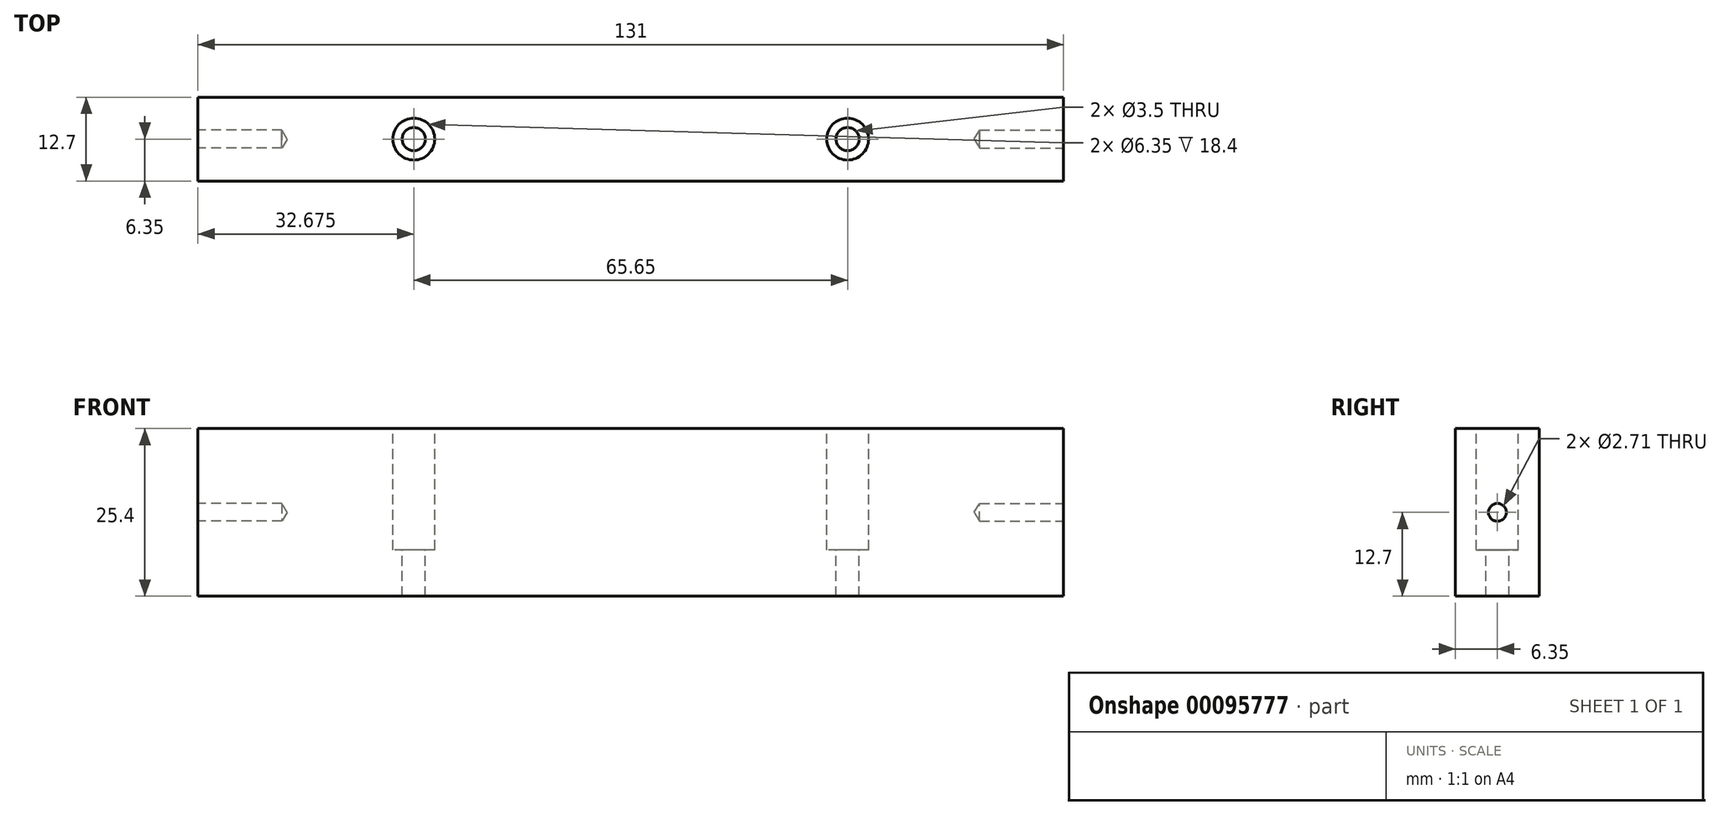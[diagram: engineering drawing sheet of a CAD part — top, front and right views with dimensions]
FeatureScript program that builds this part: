
annotation { "Feature Type Name" : "Feature", "Feature Type Description" : "" }
export const myFeature = defineFeature(function(context is Context, id is Id, definition is map)
    precondition{}
    {
        {
            var Q0;
            Q0=qCreatedBy(makeId("Right.planeOp"),FACE);
            var sketch = newSketch(context, id + "F0", { "sketchPlane" : qUnion([Q0])});
            skLineSegment(sketch, "E0.bottom", {"start": v(-6.35, -12.7) * mm, "end": v(6.35, -12.7) * mm});
            skLineSegment(sketch, "E0.top", {"start": v(-6.35, 12.7) * mm, "end": v(6.35, 12.7) * mm});
            skLineSegment(sketch, "E0.left", {"start": v(-6.35, -12.7) * mm, "end": v(-6.35, 12.7) * mm});
            skLineSegment(sketch, "E0.right", {"start": v(6.35, -12.7) * mm, "end": v(6.35, 12.7) * mm});
            skPoint(sketch, "E0.middle", {"position": v(0, 0) * mm});
            skSolve(sketch);
        }
        {
            var Q0;
            Q0 = qSketchRegion(id + "F0", true);
            extrude(context, id + "F1", {"entities" : qUnion([Q0]), "depth" : 131 * mm});
        }
        {
            var Q0;
            Q0=makeQuery(id+"F1.opExtrude","SWEPT_FACE",FACE,{"disambiguationData":[OSD([sQuery(id+"F0.wireOp",EDGE,"E0.top")])]});
            var sketch = newSketch(context, id + "F2", { "sketchPlane" : qUnion([Q0])});
            skPoint(sketch, "E1", {"position": v(32.67, 0) * mm});
            skPoint(sketch, "E2", {"position": v(98.33, 0) * mm});
            skLineSegment(sketch, "E3", {"start": v(65.5, -6.35) * mm, "end": v(65.5, 6.35) * mm, "construction": true});
            skSolve(sketch);
        }
        {
            var Q0;
            Q0=sQuery(id+"F2.wireOp",VERTEX,"E1");
            var Q1;
            Q1=sQuery(id+"F2.wireOp",VERTEX,"E2");
            var Q2;
            Q2=makeQuery(id+"F1.opExtrude","SWEPT_BODY",BODY,{"disambiguationData":[OSD([sQuery(id+"F0.wireOp",EDGE,"E0.bottom"),sQuery(id+"F0.wireOp",EDGE,"E0.top"),sQuery(id+"F0.wireOp",EDGE,"E0.left"),sQuery(id+"F0.wireOp",EDGE,"E0.right")])]});
            hole(context, id + "F3", {"style" : HoleStyle.C_BORE, "endStyle" : HoleEndStyle.THROUGH, "holeDiameter" : 3.5 * mm, "cBoreDiameter" : 6.35 * mm, "cBoreDepth" : 18.4 * mm, "startFromSketch" : true, "locations" : qUnion([Q0, Q1]), "scope" : qUnion([Q2]), "isTappedThrough" : true});
        }
        {
            var Q0;
            Q0=makeQuery(id+"F1.opExtrude","CAP_FACE",FACE,{"disambiguationData":[OSD([sQuery(id+"F0.wireOp",EDGE,"E0.bottom"),sQuery(id+"F0.wireOp",EDGE,"E0.top"),sQuery(id+"F0.wireOp",EDGE,"E0.left"),sQuery(id+"F0.wireOp",EDGE,"E0.right")])],"isStart":false});
            var sketch = newSketch(context, id + "F4", { "sketchPlane" : qUnion([Q0])});
            skLineSegment(sketch, "E4", {"start": v(-6.35, 0) * mm, "end": v(6.35, 0) * mm, "construction": true});
            skPoint(sketch, "E5", {"position": v(0, 0) * mm});
            skSolve(sketch);
        }
        {
            var Q0;
            Q0=sQuery(id+"F4.wireOp",VERTEX,"E5");
            var Q1;
            Q1=makeQuery(id+"F1.opExtrude","SWEPT_BODY",BODY,{"disambiguationData":[OSD([sQuery(id+"F0.wireOp",EDGE,"E0.bottom"),sQuery(id+"F0.wireOp",EDGE,"E0.top"),sQuery(id+"F0.wireOp",EDGE,"E0.left"),sQuery(id+"F0.wireOp",EDGE,"E0.right")])]});
            hole(context, id + "F5", {"style" : HoleStyle.SIMPLE, "endStyle" : HoleEndStyle.BLIND, "standardTappedOrClearance" : lookupTablePath({ "standard" : "ANSI", "engagement" : "75%", "pitch" : "32 tpi", "size" : "#6", "type" : "Tapped" }), "standardBlindInLast" : lookupTablePath({ "standard" : "ANSI", "engagement" : "75%", "pitch" : "32 tpi", "size" : "#6", "type" : "Tapped" }), "holeDiameter" : 2.7 * mm, "holeDepth" : 12.7 * mm, "startFromSketch" : true, "locations" : qUnion([Q0]), "scope" : qUnion([Q1]), "majorDiameter" : 3.5 * mm});
        }
        {
            var Q0;
            Q0=makeQuery(id+"F1.opExtrude","CAP_FACE",FACE,{"disambiguationData":[OSD([sQuery(id+"F0.wireOp",EDGE,"E0.bottom"),sQuery(id+"F0.wireOp",EDGE,"E0.top"),sQuery(id+"F0.wireOp",EDGE,"E0.left"),sQuery(id+"F0.wireOp",EDGE,"E0.right")])],"isStart":true});
            var sketch = newSketch(context, id + "F6", { "sketchPlane" : qUnion([Q0])});
            skLineSegment(sketch, "E6", {"start": v(-6.35, 0) * mm, "end": v(6.35, 0) * mm, "construction": true});
            skPoint(sketch, "E7", {"position": v(0, 0) * mm});
            skSolve(sketch);
        }
        {
            var Q0;
            Q0=sQuery(id+"F6.wireOp",VERTEX,"E7");
            var Q1;
            Q1=makeQuery(id+"F1.opExtrude","SWEPT_BODY",BODY,{"disambiguationData":[OSD([sQuery(id+"F0.wireOp",EDGE,"E0.bottom"),sQuery(id+"F0.wireOp",EDGE,"E0.top"),sQuery(id+"F0.wireOp",EDGE,"E0.left"),sQuery(id+"F0.wireOp",EDGE,"E0.right")])]});
            hole(context, id + "F7", {"style" : HoleStyle.SIMPLE, "endStyle" : HoleEndStyle.BLIND, "standardTappedOrClearance" : lookupTablePath({ "standard" : "ANSI", "engagement" : "75%", "pitch" : "32 tpi", "size" : "#6", "type" : "Tapped" }), "standardBlindInLast" : lookupTablePath({ "standard" : "ANSI", "engagement" : "75%", "pitch" : "32 tpi", "size" : "#6", "type" : "Tapped" }), "holeDiameter" : 2.7 * mm, "holeDepth" : 12.7 * mm, "startFromSketch" : true, "locations" : qUnion([Q0]), "scope" : qUnion([Q1]), "majorDiameter" : 3.5 * mm});
        }
    });
